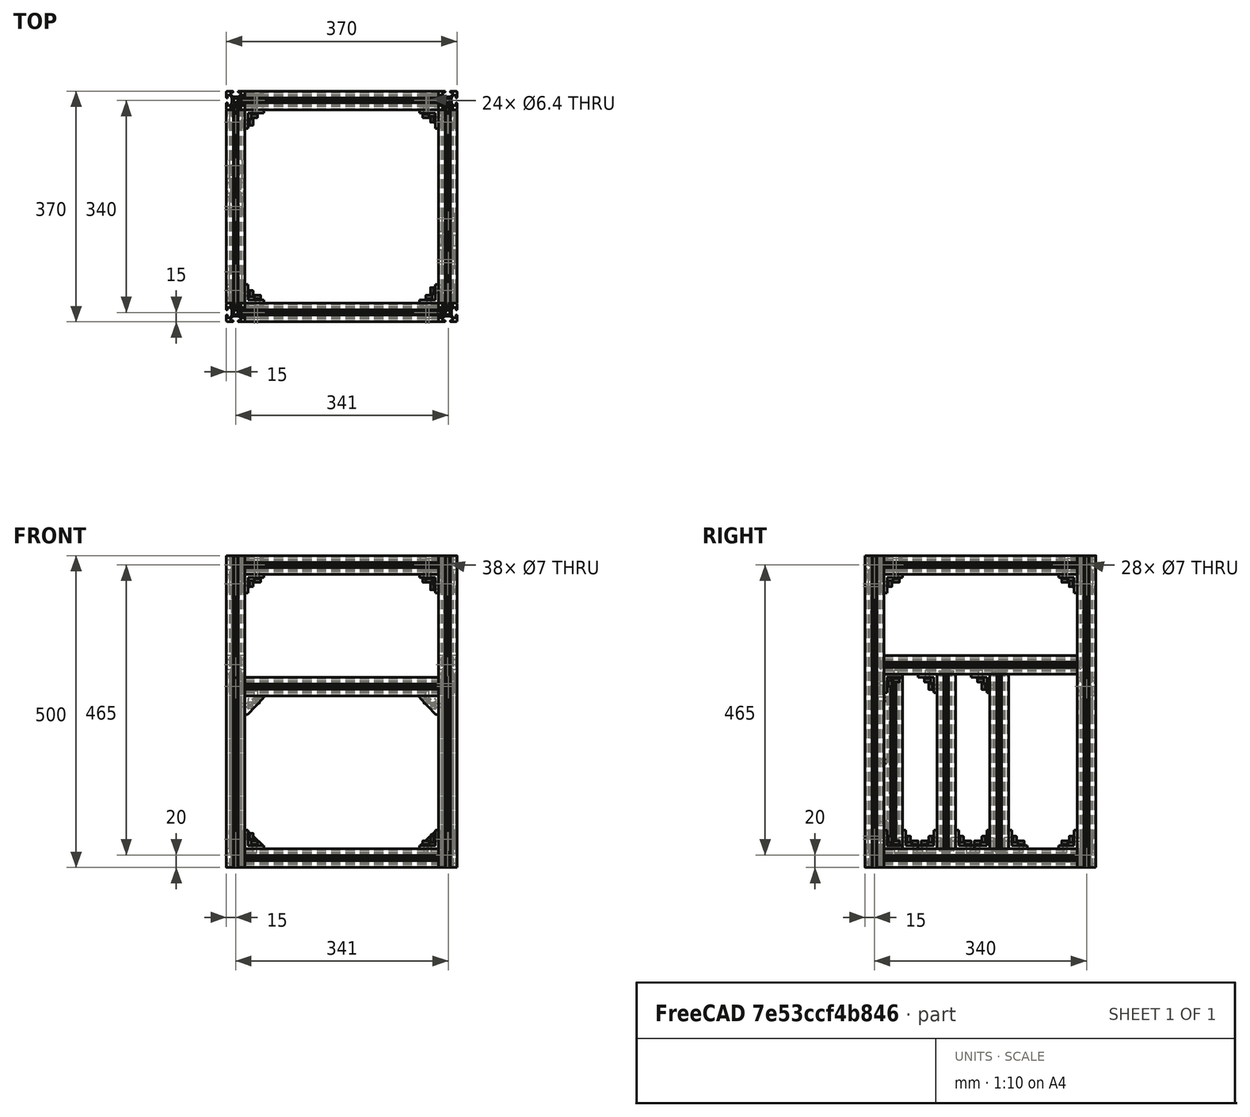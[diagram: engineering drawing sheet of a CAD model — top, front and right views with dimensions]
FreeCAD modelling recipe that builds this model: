
FCSTD DOCUMENT  (FreeCAD 0.19R24291 (Git))
Label: frame-assembly
License: Other
LicenseURL: GPL3
objects: Part::FeaturePython×141, Part::Feature×68, App::Part×4, PartDesign::CoordinateSystem×1
note: 210 computed .brp shape members not serialized (recipe doc carries the construction recipe); baked Part::Feature solids carry a one-line shape summary decoded from their .brp

FEATURE [Part::Feature] Extrude001  label="3030-310mm001-tap"
  Placement = pos=(-155,15,15) rot=(0,1,0;1.5708rad)
  shape: bbox 310 x 30 x 30 mm, 95 faces (baked)
FEATURE [Part::Feature] Extrude002  label="3030-310mm002-tap"
  Placement = pos=(-155,355,15) rot=(0,1,0;1.5708rad)
  shape: bbox 310 x 30 x 30 mm, 95 faces (baked)
FEATURE [Part::Feature] Extrude005  label="3030-310mm003-tap"
  Placement = pos=(170,30,485) rot=(0.57735,-0.57735,-0.57735;4.18879rad)
  shape: bbox 30 x 310 x 30 mm, 95 faces (baked)
FEATURE [Part::Feature] Extrude006  label="3030-310mm004-tap"
  Placement = pos=(-170,30,485) rot=(0.57735,-0.57735,-0.57735;4.18879rad)
  shape: bbox 30 x 310 x 30 mm, 95 faces (baked)
FEATURE [Part::Feature] Extrude007  label="3030-310mm005-tap"
  Placement = pos=(-155,355,485) rot=(0,1,0;1.5708rad)
  shape: bbox 310 x 30 x 30 mm, 95 faces (baked)
FEATURE [Part::Feature] Extrude008  label="3030-310mm006-tap"
  Placement = pos=(-155,15,485) rot=(0,1,0;1.5708rad)
  shape: bbox 310 x 30 x 30 mm, 95 faces (baked)
FEATURE [Part::Feature] Extrude010  label="3030-310mm007-tap"
  Placement = pos=(-155,355,290) rot=(0,1,0;1.5708rad)
  shape: bbox 310 x 30 x 30 mm, 95 faces (baked)
FEATURE [Part::Feature] Extrude002002002002  label="3030-280mm001-tap"
  Placement = pos=(-170,215,30) rot=(0,0,1;0rad)
  shape: bbox 30 x 30 x 280 mm, 95 faces (baked)
FEATURE [Part::Feature] Extrude002002002003  label="3030-280mm002-tap"
  Placement = pos=(170,130,30) rot=(0,0,1;0rad)
  shape: bbox 30 x 30 x 280 mm, 95 faces (baked)
FEATURE [Part::Feature] Cut008004003004014002002003  label="3030-280mm003-tap"
  Placement = pos=(-170,45,30) rot=(0,0,1;0rad)
  shape: bbox 30 x 30 x 280 mm, 137 faces (baked)
FEATURE [Part::Feature] Cut008004003004014002002011  label="3030-310mm008-tap-drill"
  Placement = pos=(-170,30,0) rot=(0,0,1;0rad)
  shape: bbox 30 x 310 x 30 mm, 109 faces (baked)
FEATURE [Part::Feature] Cut008004003004014002002012  label="3030-310mm009-tap-drill"
  Placement = pos=(-170,30,310) rot=(0,0,1;0rad)
  shape: bbox 30 x 310 x 30 mm, 109 faces (baked)
FEATURE [Part::Feature] Cut008004003004014002002013  label="3030-310mm010-tap-drill"
  Placement = pos=(170,30,0) rot=(0,0,1;0rad)
  shape: bbox 30 x 310 x 30 mm, 109 faces (baked)
FEATURE [Part::Feature] Cut008004003004014002002014  label="3030-310mm011-tap-drill"
  Placement = pos=(170,30,310) rot=(0,0,1;0rad)
  shape: bbox 30 x 310 x 30 mm, 109 faces (baked)
FEATURE [Part::Feature] Part__Feature112001022  label="Block-corner-bracket003"
  Placement = pos=(155,355,275) rot=(0.57735,0.57735,-0.57735;4.18879rad)
  shape: bbox 31 x 20 x 31 mm, 71 faces (baked)
FEATURE [Part::Feature] Part__Feature112001023  label="Block-corner-bracket004"
  Placement = pos=(-155,355,275) rot=(0.57735,-0.57735,0.57735;4.18879rad)
  shape: bbox 31 x 20 x 31 mm, 71 faces (baked)
FEATURE [Part::Feature] Part__Feature008  label="L-corner-bracket001"
  Placement = pos=(-155,15,30) rot=(0,0,-1;1.5708rad)
  shape: bbox 30 x 20 x 30 mm, 10 faces (baked)
FEATURE [Part::Feature] Part__Feature112001040  label="L-corner-bracket002"
  Placement = pos=(-155,15,470) rot=(0.57735,-0.57735,0.57735;4.18879rad)
  shape: bbox 30 x 20 x 30 mm, 10 faces (baked)
FEATURE [Part::Feature] Part__Feature112001041  label="L-corner-bracket003"
  Placement = pos=(155,15,470) rot=(0.707107,-0.707107,0;3.14159rad)
  shape: bbox 30 x 20 x 30 mm, 10 faces (baked)
FEATURE [Part::Feature] Part__Feature112001042  label="L-corner-bracket004"
  Placement = pos=(155,15,30) rot=(0.57735,-0.57735,-0.57735;2.0944rad)
  shape: bbox 30 x 20 x 30 mm, 10 faces (baked)
FEATURE [Part::Feature] Part__Feature112001054  label="HCJ_Joint001"
  Placement = pos=(-159,355,290) rot=(0.57735,0.57735,-0.57735;2.0944rad)
  shape: bbox 7.5 x 15 x 24 mm, 29 faces (baked)
FEATURE [Part::Feature] Part__Feature112001055  label="HCJ_Joint002"
  Placement = pos=(160,355,290) rot=(0.57735,-0.57735,-0.57735;4.18879rad)
  shape: bbox 7.5 x 15 x 24 mm, 29 faces (baked)
FEATURE [Part::Feature] Part__Feature112001056  label="HCJ_Joint003"
  Placement = pos=(-159,355,485) rot=(0.57735,0.57735,-0.57735;2.0944rad)
  shape: bbox 7.5 x 15 x 24 mm, 29 faces (baked)
FEATURE [Part::Feature] Part__Feature112001057  label="HCJ_Joint004"
  Placement = pos=(160,355,485) rot=(0.57735,-0.57735,-0.57735;4.18879rad)
  shape: bbox 7.5 x 15 x 24 mm, 29 faces (baked)
FEATURE [Part::Feature] Part__Feature112001058  label="HCJ_Joint005"
  Placement = pos=(-159,355,15) rot=(0.57735,0.57735,-0.57735;2.0944rad)
  shape: bbox 7.5 x 15 x 24 mm, 29 faces (baked)
FEATURE [Part::Feature] Part__Feature112001059  label="HCJ_Joint006"
  Placement = pos=(160,355,15) rot=(0.57735,-0.57735,-0.57735;4.18879rad)
  shape: bbox 7.5 x 15 x 24 mm, 29 faces (baked)
FEATURE [Part::Feature] Part__Feature112001060  label="HCJ_Joint007"
  Placement = pos=(170,344,15) rot=(0.707107,0,-0.707107;3.14159rad)
  shape: bbox 15 x 7.5 x 24 mm, 29 faces (baked)
FEATURE [Part::Feature] Part__Feature112001061  label="HCJ_Joint008"
  Placement = pos=(170,26,15) rot=(0,1,0;1.5708rad)
  shape: bbox 15 x 7.5 x 24 mm, 29 faces (baked)
FEATURE [Part::Feature] Part__Feature112001062  label="HCJ_Joint009"
  Placement = pos=(159,15,15) rot=(0.57735,-0.57735,-0.57735;4.18879rad)
  shape: bbox 7.5 x 15 x 24 mm, 29 faces (baked)
FEATURE [Part::Feature] Part__Feature112001063  label="HCJ_Joint010"
  Placement = pos=(-159,15,15) rot=(0.57735,0.57735,-0.57735;2.0944rad)
  shape: bbox 7.5 x 15 x 24 mm, 29 faces (baked)
FEATURE [Part::Feature] Part__Feature112001064  label="HCJ_Joint011"
  Placement = pos=(-170,26,15) rot=(0,1,0;1.5708rad)
  shape: bbox 15 x 7.5 x 24 mm, 29 faces (baked)
FEATURE [Part::Feature] Part__Feature112001065  label="HCJ_Joint012"
  Placement = pos=(-170,344,485) rot=(0.707107,0,-0.707107;3.14159rad)
  shape: bbox 15 x 7.5 x 24 mm, 29 faces (baked)
FEATURE [Part::Feature] Part__Feature112001066  label="HCJ_Joint013"
  Placement = pos=(170,344,485) rot=(0.707107,0,-0.707107;3.14159rad)
  shape: bbox 15 x 7.5 x 24 mm, 29 faces (baked)
FEATURE [Part::Feature] Part__Feature112001067  label="HCJ_Joint014"
  Placement = pos=(170,26,485) rot=(0,1,0;1.5708rad)
  shape: bbox 15 x 7.5 x 24 mm, 29 faces (baked)
FEATURE [Part::Feature] Part__Feature112001068  label="HCJ_Joint015"
  Placement = pos=(159,15,485) rot=(0.57735,-0.57735,-0.57735;4.18879rad)
  shape: bbox 7.5 x 15 x 24 mm, 29 faces (baked)
FEATURE [Part::Feature] Part__Feature112001069  label="HCJ_Joint016"
  Placement = pos=(-159,15,485) rot=(0.57735,0.57735,-0.57735;2.0944rad)
  shape: bbox 7.5 x 15 x 24 mm, 29 faces (baked)
FEATURE [Part::Feature] Part__Feature112001070  label="HCJ_Joint017"
  Placement = pos=(-170,26,485) rot=(0,1,0;1.5708rad)
  shape: bbox 15 x 7.5 x 24 mm, 29 faces (baked)
FEATURE [Part::Feature] Part__Feature112001071  label="L-corner-bracket005"
  Placement = pos=(-155,30,485) rot=(0,1,0;1.5708rad)
  shape: bbox 30 x 30 x 20 mm, 10 faces (baked)
FEATURE [Part::Feature] Part__Feature112001072  label="L-corner-bracket006"
  Placement = pos=(-155,340,485) rot=(0.57735,0.57735,-0.57735;2.0944rad)
  shape: bbox 30 x 30 x 20 mm, 10 faces (baked)
FEATURE [Part::Feature] Part__Feature112001073  label="L-corner-bracket007"
  Placement = pos=(155,340,485) rot=(0.707107,0,-0.707107;3.14159rad)
  shape: bbox 30 x 30 x 20 mm, 10 faces (baked)
FEATURE [Part::Feature] Part__Feature112001074  label="L-corner-bracket008"
  Placement = pos=(155,30,485) rot=(0.57735,-0.57735,-0.57735;4.18879rad)
  shape: bbox 30 x 30 x 20 mm, 10 faces (baked)
FEATURE [Part::Feature] Part__Feature112001020  label="Block-corner-bracket001"
  Placement = pos=(-155,355,30) rot=(0,0,-1;1.5708rad)
  shape: bbox 31 x 20 x 31 mm, 71 faces (baked)
FEATURE [Part::Feature] Part__Feature112001021  label="Block-corner-bracket002"
  Placement = pos=(155,355,30) rot=(0,0,1;1.5708rad)
  shape: bbox 31 x 20 x 31 mm, 71 faces (baked)
FEATURE [Part::Feature] Part__Feature112001075  label="L-corner-bracket009"
  Placement = pos=(155,355,470) rot=(0.57735,0.57735,-0.57735;4.18879rad)
  shape: bbox 30 x 20 x 30 mm, 10 faces (baked)
FEATURE [Part::Feature] Part__Feature112001078  label="L-corner-bracket011"
  Placement = pos=(170,30,30) rot=(0,0.707107,0.707107;3.14159rad)
  shape: bbox 20 x 30 x 30 mm, 10 faces (baked)
FEATURE [Part::Feature] Part__Feature112001079  label="L-corner-bracket012"
  Placement = pos=(-170,200,30) rot=(1,0,0;1.5708rad)
  shape: bbox 20 x 30 x 30 mm, 10 faces (baked)
FEATURE [Part::Feature] Part__Feature112001080  label="L-corner-bracket013"
  Placement = pos=(171,115,30) rot=(1,0,0;1.5708rad)
  shape: bbox 20 x 30 x 30 mm, 10 faces (baked)
FEATURE [Part::Feature] Part__Feature112001081  label="L-corner-bracket014"
  Placement = pos=(-170,200,310) rot=(1,0,0;3.14159rad)
  shape: bbox 20 x 30 x 30 mm, 10 faces (baked)
FEATURE [Part::Feature] Part__Feature112001082  label="L-corner-bracket016"
  Placement = pos=(171,115,310) rot=(1,0,0;3.14159rad)
  shape: bbox 20 x 30 x 30 mm, 10 faces (baked)
FEATURE [Part::Feature] Part__Feature112001083  label="L-corner-bracket015"
  Placement = pos=(171,30,310) rot=(-1,0,0;1.5708rad)
  shape: bbox 20 x 30 x 30 mm, 10 faces (baked)
FEATURE [Part::Feature] Part__Feature112001084  label="L-corner-bracket018"
  Placement = pos=(171,145,30) rot=(0,0.707107,0.707107;3.14159rad)
  shape: bbox 20 x 30 x 30 mm, 10 faces (baked)
FEATURE [Part::Feature] Part__Feature112001085  label="L-corner-bracket017"
  Placement = pos=(-170,230,30) rot=(0,0.707107,0.707107;3.14159rad)
  shape: bbox 20 x 30 x 30 mm, 10 faces (baked)
FEATURE [Part::Feature] Part__Feature112001086  label="L-corner-bracket020"
  Placement = pos=(-170,60,30) rot=(0,0.707107,0.707107;3.14159rad)
  shape: bbox 20 x 30 x 30 mm, 10 faces (baked)
FEATURE [Part::Feature] Part__Feature112001087  label="HCJ_Joint018"
  Placement = pos=(-170,344,15) rot=(0.707107,0,-0.707107;3.14159rad)
  shape: bbox 15 x 7.5 x 24 mm, 29 faces (baked)
FEATURE [Part::Feature] Part__Feature112001089  label="HCJ_Joint019"
  Placement = pos=(-170,214.5,27) rot=(0.57735,-0.57735,-0.57735;2.0944rad)
  shape: bbox 15 x 24 x 7.5 mm, 29 faces (baked)
FEATURE [Part::Feature] Part__Feature112001090  label="HCJ_Joint020"
  Placement = pos=(-170,214.5,315) rot=(0.57735,0.57735,-0.57735;4.18879rad)
  shape: bbox 15 x 24 x 7.5 mm, 29 faces (baked)
FEATURE [Part::Feature] Part__Feature112001091  label="HCJ_Joint021"
  Placement = pos=(170,130.5,315) rot=(0.57735,0.57735,-0.57735;4.18879rad)
  shape: bbox 15 x 24 x 7.5 mm, 29 faces (baked)
FEATURE [Part::Feature] Part__Feature112001092  label="HCJ_Joint022"
  Placement = pos=(170,130.5,27) rot=(0.57735,-0.57735,-0.57735;2.0944rad)
  shape: bbox 15 x 24 x 7.5 mm, 29 faces (baked)
FEATURE [App::Part] Part049  label="HCJ-joint"
  Group = -> [Part__Feature112001054,Part__Feature112001055,Part__Feature112001056,Part__Feature112001057,Part__Feature112001058,Part__Feature112001059,Part__Feature112001060,Part__Feature112001061,Part__Feature112001062,Part__Feature112001063,Part__Feature112001064,Part__Feature112001065,Part__Feature112001066,Part__Feature112001067,Part__Feature112001068,Part__Feature112001069,Part__Feature112001070,+5 more]
  Origin = -> Origin051
FEATURE [Part::Feature] Part__Feature112001088  label="L-corner-bracket021"
  Placement = pos=(171,340,30) rot=(1,0,0;1.5708rad)
  shape: bbox 20 x 30 x 30 mm, 10 faces (baked)
FEATURE [Part::FeaturePython] Screw  label="M8x20-Screw"  # Fasteners workbench fastener (typed FeaturePython)
  Placement = pos=(170,344,485) rot=(-1,0,0;1.5708rad)
  baseObject = -> Extrude005 [Edge279]
  diameter = 5
  invert = false
  length = 3
  lengthCustom = 20
  matchOuter = false
  offset = 4
  thread = false
  type = 39
FEATURE [Part::FeaturePython] Screw001  label="M8x20-Screw057"  # Fasteners workbench fastener (typed FeaturePython)
  Placement = pos=(159,355,485) rot=(0,1,0;1.5708rad)
  baseObject = -> Extrude007 [Edge279]
  diameter = 5
  invert = false
  length = 3
  lengthCustom = 20
  matchOuter = false
  offset = 4
  thread = false
  type = 39
FEATURE [Part::FeaturePython] Screw002  label="M8x20-Screw007"  # Fasteners workbench fastener (typed FeaturePython)
  Placement = pos=(170,344,325) rot=(-1,0,0;1.5708rad)
  baseObject = -> Cut008004003004014002002014 [Edge190]
  diameter = 5
  invert = false
  length = 3
  lengthCustom = 20
  matchOuter = false
  offset = 4
  thread = false
  type = 39
FEATURE [Part::FeaturePython] Screw003  label="M8x20-Screw008"  # Fasteners workbench fastener (typed FeaturePython)
  Placement = pos=(159,355,290) rot=(0,1,0;1.5708rad)
  baseObject = -> Extrude010 [Edge279]
  diameter = 5
  invert = false
  length = 3
  lengthCustom = 20
  matchOuter = false
  offset = 4
  thread = false
  type = 39
FEATURE [Part::FeaturePython] Screw004  label="M8x20-Screw009"  # Fasteners workbench fastener (typed FeaturePython)
  Placement = pos=(170,344,15) rot=(-1,0,0;1.5708rad)
  baseObject = -> Cut008004003004014002002013 [Edge190]
  diameter = 5
  invert = false
  length = 3
  lengthCustom = 20
  matchOuter = false
  offset = 4
  thread = false
  type = 39
FEATURE [Part::FeaturePython] Screw005  label="M8x20-Screw010"  # Fasteners workbench fastener (typed FeaturePython)
  Placement = pos=(159,355,15) rot=(0,1,0;1.5708rad)
  baseObject = -> Extrude002 [Edge279]
  diameter = 5
  invert = false
  length = 3
  lengthCustom = 20
  matchOuter = false
  offset = 4
  thread = false
  type = 39
FEATURE [Part::FeaturePython] Screw006  label="M8x20-Screw058"  # Fasteners workbench fastener (typed FeaturePython)
  Placement = pos=(-159,355,485) rot=(0,-1,0;1.5708rad)
  baseObject = -> Extrude007 [Edge278]
  diameter = 5
  invert = true
  length = 3
  lengthCustom = 20
  matchOuter = false
  offset = 4
  thread = false
  type = 39
FEATURE [Part::FeaturePython] Screw007  label="M8x20-Screw054"  # Fasteners workbench fastener (typed FeaturePython)
  Placement = pos=(-170,344,485) rot=(-1,0,0;1.5708rad)
  baseObject = -> Extrude006 [Edge279]
  diameter = 5
  invert = false
  length = 3
  lengthCustom = 20
  matchOuter = false
  offset = 4
  thread = false
  type = 39
FEATURE [Part::FeaturePython] Screw008  label="M8x20-Screw019"  # Fasteners workbench fastener (typed FeaturePython)
  Placement = pos=(-170,344,325) rot=(-1,0,0;1.5708rad)
  baseObject = -> Cut008004003004014002002012 [Edge190]
  diameter = 5
  invert = false
  length = 3
  lengthCustom = 20
  matchOuter = false
  offset = 4
  thread = false
  type = 39
FEATURE [Part::FeaturePython] Screw009  label="M8x20-Screw024"  # Fasteners workbench fastener (typed FeaturePython)
  Placement = pos=(-159,355,290) rot=(0,-1,0;1.5708rad)
  baseObject = -> Extrude010 [Edge278]
  diameter = 5
  invert = true
  length = 3
  lengthCustom = 20
  matchOuter = false
  offset = 4
  thread = false
  type = 39
FEATURE [Part::FeaturePython] Screw010  label="M8x20-Screw025"  # Fasteners workbench fastener (typed FeaturePython)
  Placement = pos=(-159,355,15) rot=(0,-1,0;1.5708rad)
  baseObject = -> Extrude002 [Edge278]
  diameter = 5
  invert = true
  length = 3
  lengthCustom = 20
  matchOuter = false
  offset = 4
  thread = false
  type = 39
FEATURE [Part::FeaturePython] Screw011  label="M8x20-Screw022"  # Fasteners workbench fastener (typed FeaturePython)
  Placement = pos=(-170,344,15) rot=(-1,0,0;1.5708rad)
  baseObject = -> Cut008004003004014002002011 [Edge190]
  diameter = 5
  invert = false
  length = 3
  lengthCustom = 20
  matchOuter = false
  offset = 4
  thread = false
  type = 39
FEATURE [Part::FeaturePython] Screw012  label="M8x20-Screw053"  # Fasteners workbench fastener (typed FeaturePython)
  Placement = pos=(-170,26,485) rot=(1,0,0;1.5708rad)
  baseObject = -> Extrude006 [Edge278]
  diameter = 5
  invert = true
  length = 15
  lengthCustom = 20
  matchOuter = false
  offset = 4
  thread = false
  type = 39
FEATURE [Part::FeaturePython] Screw013  label="M8x20-Screw055"  # Fasteners workbench fastener (typed FeaturePython)
  Placement = pos=(-159,15,485) rot=(0,-1,0;1.5708rad)
  baseObject = -> Extrude008 [Edge278]
  diameter = 5
  invert = true
  length = 15
  lengthCustom = 20
  matchOuter = false
  offset = 4
  thread = false
  type = 39
FEATURE [Part::FeaturePython] Screw014  label="M8x20-Screw033"  # Fasteners workbench fastener (typed FeaturePython)
  Placement = pos=(-170,26,325) rot=(1,0,0;1.5708rad)
  baseObject = -> Cut008004003004014002002012 [Edge100]
  diameter = 5
  invert = true
  length = 15
  lengthCustom = 20
  matchOuter = false
  offset = 4
  thread = false
  type = 39
FEATURE [Part::FeaturePython] Screw015  label="M8x20-Screw034"  # Fasteners workbench fastener (typed FeaturePython)
  Placement = pos=(-170,26,15) rot=(1,0,0;1.5708rad)
  baseObject = -> Cut008004003004014002002011 [Edge100]
  diameter = 5
  invert = true
  length = 15
  lengthCustom = 20
  matchOuter = false
  offset = 4
  thread = false
  type = 39
FEATURE [Part::FeaturePython] Screw016  label="M8x20-Screw035"  # Fasteners workbench fastener (typed FeaturePython)
  Placement = pos=(-159,15,15) rot=(0,-1,0;1.5708rad)
  baseObject = -> Extrude001 [Edge278]
  diameter = 5
  invert = true
  length = 15
  lengthCustom = 20
  matchOuter = false
  offset = 4
  thread = false
  type = 39
FEATURE [Part::FeaturePython] Screw017  label="M8x20-Screw056"  # Fasteners workbench fastener (typed FeaturePython)
  Placement = pos=(159,15,485) rot=(0,1,0;1.5708rad)
  baseObject = -> Extrude008 [Edge279]
  diameter = 5
  invert = false
  length = 3
  lengthCustom = 20
  matchOuter = false
  offset = 4
  thread = false
  type = 39
FEATURE [Part::FeaturePython] Screw018  label="M8x20-Screw059"  # Fasteners workbench fastener (typed FeaturePython)
  Placement = pos=(170,26,485) rot=(1,0,0;1.5708rad)
  baseObject = -> Extrude005 [Edge278]
  diameter = 5
  invert = true
  length = 3
  lengthCustom = 20
  matchOuter = false
  offset = 4
  thread = false
  type = 39
FEATURE [Part::FeaturePython] Screw019  label="M8x20-Screw047"  # Fasteners workbench fastener (typed FeaturePython)
  Placement = pos=(170,26,325) rot=(1,0,0;1.5708rad)
  baseObject = -> Cut008004003004014002002014 [Edge100]
  diameter = 5
  invert = true
  length = 3
  lengthCustom = 20
  matchOuter = false
  offset = 4
  thread = false
  type = 39
FEATURE [Part::FeaturePython] Screw020  label="M8x20-Screw044"  # Fasteners workbench fastener (typed FeaturePython)
  Placement = pos=(159,15,15) rot=(0,1,0;1.5708rad)
  baseObject = -> Extrude001 [Edge279]
  diameter = 5
  invert = false
  length = 3
  lengthCustom = 20
  matchOuter = false
  offset = 4
  thread = false
  type = 39
FEATURE [Part::FeaturePython] Screw021  label="M8x20-Screw048"  # Fasteners workbench fastener (typed FeaturePython)
  Placement = pos=(170,26,15) rot=(1,0,0;1.5708rad)
  baseObject = -> Cut008004003004014002002013 [Edge100]
  diameter = 5
  invert = true
  length = 3
  lengthCustom = 20
  matchOuter = false
  offset = 4
  thread = false
  type = 39
FEATURE [Part::FeaturePython] Washer  label="M6-Washer"  # Fasteners workbench fastener (typed FeaturePython)
  Placement = pos=(-150,15,455) rot=(0,1,0;1.5708rad)
  baseObject = -> Part__Feature112001040 [Edge7]
  diameter = 2
  invert = true
  matchOuter = true
  offset = 0
  type = 4
FEATURE [Part::FeaturePython] Washer001  label="M6-Washer119"  # Fasteners workbench fastener (typed FeaturePython)
  Placement = pos=(-135,15,465) rot=(1,0,0;3.14159rad)
  baseObject = -> Part__Feature112001040 [Edge1]
  diameter = 2
  invert = true
  matchOuter = true
  offset = 0
  type = 4
FEATURE [Part::FeaturePython] Washer002  label="M6-Washer114"  # Fasteners workbench fastener (typed FeaturePython)
  Placement = pos=(140,15,465) rot=(1,0,0;3.14159rad)
  baseObject = -> Part__Feature112001041 [Edge7]
  diameter = 2
  invert = true
  matchOuter = true
  offset = 0
  type = 4
FEATURE [Part::FeaturePython] Washer003  label="M6-Washer113"  # Fasteners workbench fastener (typed FeaturePython)
  Placement = pos=(150,15,450) rot=(0,-1,0;1.5708rad)
  baseObject = -> Part__Feature112001041 [Edge1]
  diameter = 2
  invert = true
  matchOuter = true
  offset = 0
  type = 4
FEATURE [Part::FeaturePython] Washer004  label="M6-Washer011"  # Fasteners workbench fastener (typed FeaturePython)
  Placement = pos=(150,15,45) rot=(0,-1,0;1.5708rad)
  baseObject = -> Part__Feature112001042 [Edge7]
  diameter = 2
  invert = true
  matchOuter = true
  offset = 0
  type = 4
FEATURE [Part::FeaturePython] Washer005  label="M6-Washer012"  # Fasteners workbench fastener (typed FeaturePython)
  Placement = pos=(135,15,35) rot=(0,0,1;0rad)
  baseObject = -> Part__Feature112001042 [Edge1]
  diameter = 2
  invert = true
  matchOuter = true
  offset = 0
  type = 4
FEATURE [Part::FeaturePython] Washer006  label="M6-Washer013"  # Fasteners workbench fastener (typed FeaturePython)
  Placement = pos=(-150,15,50) rot=(0,1,0;1.5708rad)
  baseObject = -> Part__Feature008 [Edge4]
  diameter = 2
  invert = true
  matchOuter = true
  offset = 0
  type = 4
FEATURE [Part::FeaturePython] Washer007  label="M6-Washer014"  # Fasteners workbench fastener (typed FeaturePython)
  Placement = pos=(-140,15,35) rot=(0,0,1;0rad)
  baseObject = -> Part__Feature008 [Edge7]
  diameter = 2
  invert = true
  matchOuter = true
  offset = 0
  type = 4
FEATURE [Part::FeaturePython] Washer008  label="M6-Washer027"  # Fasteners workbench fastener (typed FeaturePython)
  Placement = pos=(171,50,305) rot=(1,0,0;3.14159rad)
  baseObject = -> Part__Feature112001083 [Edge1]
  diameter = 2
  invert = true
  matchOuter = true
  offset = 0
  type = 4
FEATURE [Part::FeaturePython] Washer009  label="M6-Washer028"  # Fasteners workbench fastener (typed FeaturePython)
  Placement = pos=(171,35,295) rot=(-1,0,0;1.5708rad)
  baseObject = -> Part__Feature112001083 [Edge7]
  diameter = 2
  invert = true
  matchOuter = true
  offset = 0
  type = 4
FEATURE [Part::FeaturePython] Washer010  label="M6-Washer029"  # Fasteners workbench fastener (typed FeaturePython)
  Placement = pos=(171,100,305) rot=(1,0,0;3.14159rad)
  baseObject = -> Part__Feature112001082 [Edge7]
  diameter = 2
  invert = true
  matchOuter = true
  offset = 0
  type = 4
FEATURE [Part::FeaturePython] Washer011  label="M6-Washer030"  # Fasteners workbench fastener (typed FeaturePython)
  Placement = pos=(171,110,290) rot=(1,0,0;1.5708rad)
  baseObject = -> Part__Feature112001082 [Edge1]
  diameter = 2
  invert = true
  matchOuter = true
  offset = 0
  type = 4
FEATURE [Part::FeaturePython] Washer012  label="M6-Washer031"  # Fasteners workbench fastener (typed FeaturePython)
  Placement = pos=(170,35,45) rot=(-1,0,0;1.5708rad)
  baseObject = -> Part__Feature112001078 [Edge7]
  diameter = 2
  invert = true
  matchOuter = true
  offset = 0
  type = 4
FEATURE [Part::FeaturePython] Washer013  label="M6-Washer032"  # Fasteners workbench fastener (typed FeaturePython)
  Placement = pos=(170,50,35) rot=(0,0,1;0rad)
  baseObject = -> Part__Feature112001078 [Edge1]
  diameter = 2
  invert = true
  matchOuter = true
  offset = 0
  type = 4
FEATURE [Part::FeaturePython] Washer014  label="M6-Washer033"  # Fasteners workbench fastener (typed FeaturePython)
  Placement = pos=(171,95,35) rot=(0,0,1;0rad)
  baseObject = -> Part__Feature112001080 [Edge4]
  diameter = 2
  invert = true
  matchOuter = true
  offset = 0
  type = 4
FEATURE [Part::FeaturePython] Washer015  label="M6-Washer034"  # Fasteners workbench fastener (typed FeaturePython)
  Placement = pos=(171,110,45) rot=(1,0,0;1.5708rad)
  baseObject = -> Part__Feature112001080 [Edge7]
  diameter = 2
  invert = true
  matchOuter = true
  offset = 0
  type = 4
FEATURE [Part::FeaturePython] Washer016  label="M6-Washer035"  # Fasteners workbench fastener (typed FeaturePython)
  Placement = pos=(171,165,35) rot=(0,0,1;0rad)
  baseObject = -> Part__Feature112001084 [Edge4]
  diameter = 2
  invert = true
  matchOuter = true
  offset = 0
  type = 4
FEATURE [Part::FeaturePython] Washer017  label="M6-Washer036"  # Fasteners workbench fastener (typed FeaturePython)
  Placement = pos=(171,150,45) rot=(-1,0,0;1.5708rad)
  baseObject = -> Part__Feature112001084 [Edge7]
  diameter = 2
  invert = true
  matchOuter = true
  offset = 0
  type = 4
FEATURE [Part::FeaturePython] Washer018  label="M6-Washer037"  # Fasteners workbench fastener (typed FeaturePython)
  Placement = pos=(171,320,35) rot=(0,0,1;0rad)
  baseObject = -> Part__Feature112001088 [Edge1]
  diameter = 2
  invert = true
  matchOuter = true
  offset = 0
  type = 4
FEATURE [Part::FeaturePython] Washer019  label="M6-Washer038"  # Fasteners workbench fastener (typed FeaturePython)
  Placement = pos=(171,335,45) rot=(1,0,0;1.5708rad)
  baseObject = -> Part__Feature112001088 [Edge7]
  diameter = 2
  invert = true
  matchOuter = true
  offset = 0
  type = 4
FEATURE [Part::FeaturePython] Washer020  label="M6-Washer039"  # Fasteners workbench fastener (typed FeaturePython)
  Placement = pos=(137,355,270.8) rot=(1,0,0;3.14159rad)
  baseObject = -> Part__Feature112001022 [Edge154]
  diameter = 2
  invert = false
  matchOuter = true
  offset = 0
  type = 4
FEATURE [Part::FeaturePython] Washer021  label="M6-Washer040"  # Fasteners workbench fastener (typed FeaturePython)
  Placement = pos=(150.5,355,260) rot=(0,-1,0;1.5708rad)
  baseObject = -> Part__Feature112001022 [Edge155]
  diameter = 2
  invert = false
  matchOuter = true
  offset = 0
  type = 4
FEATURE [Part::FeaturePython] Washer022  label="M6-Washer041"  # Fasteners workbench fastener (typed FeaturePython)
  Placement = pos=(140,355,34.5) rot=(0,0,1;0rad)
  baseObject = -> Part__Feature112001021 [Edge157]
  diameter = 2
  invert = false
  matchOuter = true
  offset = 0
  type = 4
FEATURE [Part::FeaturePython] Washer023  label="M6-Washer042"  # Fasteners workbench fastener (typed FeaturePython)
  Placement = pos=(150.8,355,48) rot=(0,-1,0;1.5708rad)
  baseObject = -> Part__Feature112001021 [Edge154]
  diameter = 2
  invert = false
  matchOuter = true
  offset = 0
  type = 4
FEATURE [Part::FeaturePython] Washer024  label="M6-Washer043"  # Fasteners workbench fastener (typed FeaturePython)
  Placement = pos=(-140,355,34.5) rot=(0,0,1;0rad)
  baseObject = -> Part__Feature112001020 [Edge155]
  diameter = 2
  invert = false
  matchOuter = true
  offset = 0
  type = 4
FEATURE [Part::FeaturePython] Washer025  label="M6-Washer044"  # Fasteners workbench fastener (typed FeaturePython)
  Placement = pos=(-150.8,355,48) rot=(0,1,0;1.5708rad)
  baseObject = -> Part__Feature112001020 [Edge153]
  diameter = 2
  invert = false
  matchOuter = true
  offset = 0
  type = 4
FEATURE [Part::FeaturePython] Washer026  label="M6-Washer045"  # Fasteners workbench fastener (typed FeaturePython)
  Placement = pos=(-150.5,355,260) rot=(0,1,0;1.5708rad)
  baseObject = -> Part__Feature112001023 [Edge155]
  diameter = 2
  invert = false
  matchOuter = true
  offset = 0
  type = 4
FEATURE [Part::FeaturePython] Washer027  label="M6-Washer046"  # Fasteners workbench fastener (typed FeaturePython)
  Placement = pos=(-137,355,270.8) rot=(1,0,0;3.14159rad)
  baseObject = -> Part__Feature112001023 [Edge153]
  diameter = 2
  invert = false
  matchOuter = true
  offset = 0
  type = 4
FEATURE [Part::FeaturePython] Washer028  label="M6-Washer055"  # Fasteners workbench fastener (typed FeaturePython)
  Placement = pos=(-170,235,45) rot=(-1,0,0;1.5708rad)
  baseObject = -> Part__Feature112001085 [Edge7]
  diameter = 2
  invert = true
  matchOuter = true
  offset = 0
  type = 4
FEATURE [Part::FeaturePython] Washer029  label="M6-Washer056"  # Fasteners workbench fastener (typed FeaturePython)
  Placement = pos=(-170,250,35) rot=(0,0,1;0rad)
  baseObject = -> Part__Feature112001085 [Edge1]
  diameter = 2
  invert = true
  matchOuter = true
  offset = 0
  type = 4
FEATURE [Part::FeaturePython] Washer030  label="M6-Washer057"  # Fasteners workbench fastener (typed FeaturePython)
  Placement = pos=(-170,180,35) rot=(0,0,1;0rad)
  baseObject = -> Part__Feature112001079 [Edge4]
  diameter = 2
  invert = true
  matchOuter = true
  offset = 0
  type = 4
FEATURE [Part::FeaturePython] Washer031  label="M6-Washer058"  # Fasteners workbench fastener (typed FeaturePython)
  Placement = pos=(-170,195,45) rot=(1,0,0;1.5708rad)
  baseObject = -> Part__Feature112001079 [Edge7]
  diameter = 2
  invert = true
  matchOuter = true
  offset = 0
  type = 4
FEATURE [Part::FeaturePython] Washer032  label="M6-Washer059"  # Fasteners workbench fastener (typed FeaturePython)
  Placement = pos=(-170,80,35) rot=(0,0,1;0rad)
  baseObject = -> Part__Feature112001086 [Edge1]
  diameter = 2
  invert = true
  matchOuter = true
  offset = 0
  type = 4
FEATURE [Part::FeaturePython] Washer033  label="M6-Washer060"  # Fasteners workbench fastener (typed FeaturePython)
  Placement = pos=(-170,65,45) rot=(-1,0,0;1.5708rad)
  baseObject = -> Part__Feature112001086 [Edge7]
  diameter = 2
  invert = true
  matchOuter = true
  offset = 0
  type = 4
FEATURE [Part::FeaturePython] Washer034  label="M6-Washer061"  # Fasteners workbench fastener (typed FeaturePython)
  Placement = pos=(-170,195,290) rot=(1,0,0;1.5708rad)
  baseObject = -> Part__Feature112001081 [Edge4]
  diameter = 2
  invert = true
  matchOuter = true
  offset = 0
  type = 4
FEATURE [Part::FeaturePython] Washer035  label="M6-Washer062"  # Fasteners workbench fastener (typed FeaturePython)
  Placement = pos=(-170,185,305) rot=(1,0,0;3.14159rad)
  baseObject = -> Part__Feature112001081 [Edge7]
  diameter = 2
  invert = true
  matchOuter = true
  offset = 0
  type = 4
FEATURE [Part::FeaturePython] Washer036  label="M6-Washer105"  # Fasteners workbench fastener (typed FeaturePython)
  Placement = pos=(135,335,485) rot=(1,0,0;1.5708rad)
  baseObject = -> Part__Feature112001073 [Edge1]
  diameter = 2
  invert = true
  matchOuter = true
  offset = 0
  type = 4
FEATURE [Part::FeaturePython] Washer037  label="M6-Washer106"  # Fasteners workbench fastener (typed FeaturePython)
  Placement = pos=(150,325,485) rot=(0,-1,0;1.5708rad)
  baseObject = -> Part__Feature112001073 [Edge7]
  diameter = 2
  invert = true
  matchOuter = true
  offset = 0
  type = 4
FEATURE [Part::FeaturePython] Washer038  label="M6-Washer112"  # Fasteners workbench fastener (typed FeaturePython)
  Placement = pos=(150,50,485) rot=(0,-1,0;1.5708rad)
  baseObject = -> Part__Feature112001074 [Edge1]
  diameter = 2
  invert = true
  matchOuter = true
  offset = 0
  type = 4
FEATURE [Part::FeaturePython] Washer039  label="M6-Washer111"  # Fasteners workbench fastener (typed FeaturePython)
  Placement = pos=(140,35,485) rot=(-1,0,0;1.5708rad)
  baseObject = -> Part__Feature112001074 [Edge7]
  diameter = 2
  invert = true
  matchOuter = true
  offset = 0
  type = 4
FEATURE [Part::FeaturePython] Washer040  label="M6-Washer116"  # Fasteners workbench fastener (typed FeaturePython)
  Placement = pos=(-135,35,485) rot=(-1,0,0;1.5708rad)
  baseObject = -> Part__Feature112001071 [Edge4]
  diameter = 2
  invert = true
  matchOuter = true
  offset = 0
  type = 4
FEATURE [Part::FeaturePython] Washer041  label="M6-Washer115"  # Fasteners workbench fastener (typed FeaturePython)
  Placement = pos=(-150,45,485) rot=(0,1,0;1.5708rad)
  baseObject = -> Part__Feature112001071 [Edge7]
  diameter = 2
  invert = true
  matchOuter = true
  offset = 0
  type = 4
FEATURE [Part::FeaturePython] Washer042  label="M6-Washer100"  # Fasteners workbench fastener (typed FeaturePython)
  Placement = pos=(-150,320,485) rot=(0,1,0;1.5708rad)
  baseObject = -> Part__Feature112001072 [Edge4]
  diameter = 2
  invert = true
  matchOuter = true
  offset = 0
  type = 4
FEATURE [Part::FeaturePython] Washer043  label="M6-Washer099"  # Fasteners workbench fastener (typed FeaturePython)
  Placement = pos=(-140,335,485) rot=(1,0,0;1.5708rad)
  baseObject = -> Part__Feature112001072 [Edge7]
  diameter = 2
  invert = true
  matchOuter = true
  offset = 0
  type = 4
FEATURE [Part::FeaturePython] Screw022  label="M6x14-Screw007"  # Fasteners workbench fastener (typed FeaturePython)
  Placement = pos=(-148.2,15,50) rot=(0,1,0;1.5708rad)
  baseObject = -> Washer006 [Edge1]
  diameter = 7
  invert = false
  length = 3
  lengthCustom = 14
  matchOuter = true
  offset = 0
  thread = false
  type = 33
FEATURE [Part::FeaturePython] Screw023  label="M6x14-Screw006"  # Fasteners workbench fastener (typed FeaturePython)
  Placement = pos=(-140,15,36.8) rot=(0,0,1;0rad)
  baseObject = -> Washer007 [Edge1]
  diameter = 7
  invert = false
  length = 3
  lengthCustom = 14
  matchOuter = true
  offset = 0
  thread = false
  type = 33
FEATURE [Part::FeaturePython] Screw024  label="M6x14-Screw005"  # Fasteners workbench fastener (typed FeaturePython)
  Placement = pos=(135,15,36.8) rot=(0,0,1;0rad)
  baseObject = -> Washer005 [Edge1]
  diameter = 7
  invert = false
  length = 3
  lengthCustom = 14
  matchOuter = true
  offset = 0
  thread = false
  type = 33
FEATURE [Part::FeaturePython] Screw025  label="M6x14-Screw004"  # Fasteners workbench fastener (typed FeaturePython)
  Placement = pos=(148.2,15,45) rot=(0,-1,0;1.5708rad)
  baseObject = -> Washer004 [Edge1]
  diameter = 7
  invert = false
  length = 3
  lengthCustom = 14
  matchOuter = true
  offset = 0
  thread = false
  type = 33
FEATURE [Part::FeaturePython] Screw026  label="M6x14-Screw074"  # Fasteners workbench fastener (typed FeaturePython)
  Placement = pos=(148.2,15,450) rot=(0,-1,0;1.5708rad)
  baseObject = -> Washer003 [Edge1]
  diameter = 7
  invert = false
  length = 3
  lengthCustom = 14
  matchOuter = true
  offset = 0
  thread = false
  type = 33
FEATURE [Part::FeaturePython] Screw027  label="M6x14-Screw075"  # Fasteners workbench fastener (typed FeaturePython)
  Placement = pos=(140,15,463.2) rot=(1,0,0;3.14159rad)
  baseObject = -> Washer002 [Edge1]
  diameter = 7
  invert = false
  length = 3
  lengthCustom = 14
  matchOuter = true
  offset = 0
  thread = false
  type = 33
FEATURE [Part::FeaturePython] Screw028  label="M6x14-Screw"  # Fasteners workbench fastener (typed FeaturePython)
  Placement = pos=(-135,15,463.2) rot=(1,0,0;3.14159rad)
  baseObject = -> Washer001 [Edge1]
  diameter = 7
  invert = false
  length = 3
  lengthCustom = 14
  matchOuter = true
  offset = 0
  thread = false
  type = 33
FEATURE [Part::FeaturePython] Screw029  label="M6x14-Screw080"  # Fasteners workbench fastener (typed FeaturePython)
  Placement = pos=(-148.2,15,455) rot=(0,1,0;1.5708rad)
  baseObject = -> Washer [Edge1]
  diameter = 7
  invert = false
  length = 3
  lengthCustom = 14
  matchOuter = true
  offset = 0
  thread = false
  type = 33
FEATURE [Part::FeaturePython] Screw030  label="M6x14-Screw015"  # Fasteners workbench fastener (typed FeaturePython)
  Placement = pos=(171,95,36.8) rot=(0,0,1;0rad)
  baseObject = -> Washer014 [Edge1]
  diameter = 7
  invert = false
  length = 3
  lengthCustom = 14
  matchOuter = true
  offset = 0
  thread = false
  type = 33
FEATURE [Part::FeaturePython] Screw031  label="M6x14-Screw014"  # Fasteners workbench fastener (typed FeaturePython)
  Placement = pos=(171,108.2,45) rot=(1,0,0;1.5708rad)
  baseObject = -> Washer015 [Edge1]
  diameter = 7
  invert = false
  length = 3
  lengthCustom = 14
  matchOuter = true
  offset = 0
  thread = false
  type = 33
FEATURE [Part::FeaturePython] Screw032  label="M6x14-Screw012"  # Fasteners workbench fastener (typed FeaturePython)
  Placement = pos=(170,50,36.8) rot=(0,0,1;0rad)
  baseObject = -> Washer013 [Edge1]
  diameter = 7
  invert = false
  length = 3
  lengthCustom = 14
  matchOuter = true
  offset = 0
  thread = false
  type = 33
FEATURE [Part::FeaturePython] Screw033  label="M6x14-Screw013"  # Fasteners workbench fastener (typed FeaturePython)
  Placement = pos=(170,36.8,45) rot=(-1,0,0;1.5708rad)
  baseObject = -> Washer012 [Edge1]
  diameter = 7
  invert = false
  length = 3
  lengthCustom = 14
  matchOuter = true
  offset = 0
  thread = false
  type = 33
FEATURE [Part::FeaturePython] Screw034  label="M6x14-Screw008"  # Fasteners workbench fastener (typed FeaturePython)
  Placement = pos=(171,50,303.2) rot=(1,0,0;3.14159rad)
  baseObject = -> Washer008 [Edge1]
  diameter = 7
  invert = false
  length = 3
  lengthCustom = 14
  matchOuter = true
  offset = 0
  thread = false
  type = 33
FEATURE [Part::FeaturePython] Screw035  label="M6x14-Screw009"  # Fasteners workbench fastener (typed FeaturePython)
  Placement = pos=(171,36.8,295) rot=(-1,0,0;1.5708rad)
  baseObject = -> Washer009 [Edge1]
  diameter = 7
  invert = false
  length = 3
  lengthCustom = 14
  matchOuter = true
  offset = 0
  thread = false
  type = 33
FEATURE [Part::FeaturePython] Screw036  label="M6x14-Screw010"  # Fasteners workbench fastener (typed FeaturePython)
  Placement = pos=(171,108.2,290) rot=(1,0,0;1.5708rad)
  baseObject = -> Washer011 [Edge1]
  diameter = 7
  invert = false
  length = 3
  lengthCustom = 14
  matchOuter = true
  offset = 0
  thread = false
  type = 33
FEATURE [Part::FeaturePython] Screw037  label="M6x14-Screw011"  # Fasteners workbench fastener (typed FeaturePython)
  Placement = pos=(171,100,303.2) rot=(1,0,0;3.14159rad)
  baseObject = -> Washer010 [Edge1]
  diameter = 7
  invert = false
  length = 3
  lengthCustom = 14
  matchOuter = true
  offset = 0
  thread = false
  type = 33
FEATURE [Part::FeaturePython] Screw040  label="M6x14-Screw022"  # Fasteners workbench fastener (typed FeaturePython)
  Placement = pos=(149,355,48) rot=(0,-1,0;1.5708rad)
  baseObject = -> Washer023 [Edge1]
  diameter = 7
  invert = false
  length = 3
  lengthCustom = 14
  matchOuter = true
  offset = 0
  thread = false
  type = 33
FEATURE [Part::FeaturePython] Screw041  label="M6x14-Screw023"  # Fasteners workbench fastener (typed FeaturePython)
  Placement = pos=(140,355,36.3) rot=(0,0,1;0rad)
  baseObject = -> Washer022 [Edge1]
  diameter = 7
  invert = false
  length = 3
  lengthCustom = 14
  matchOuter = true
  offset = 0
  thread = false
  type = 33
FEATURE [Part::FeaturePython] Screw042  label="M6x14-Screw021"  # Fasteners workbench fastener (typed FeaturePython)
  Placement = pos=(148.7,355,260) rot=(0,-1,0;1.5708rad)
  baseObject = -> Washer021 [Edge1]
  diameter = 7
  invert = false
  length = 3
  lengthCustom = 14
  matchOuter = true
  offset = 0
  thread = false
  type = 33
FEATURE [Part::FeaturePython] Screw043  label="M6x14-Screw020"  # Fasteners workbench fastener (typed FeaturePython)
  Placement = pos=(137,355,269) rot=(1,0,0;3.14159rad)
  baseObject = -> Washer020 [Edge1]
  diameter = 7
  invert = false
  length = 3
  lengthCustom = 14
  matchOuter = true
  offset = 0
  thread = false
  type = 33
FEATURE [Part::FeaturePython] Screw044  label="M6x14-Screw027"  # Fasteners workbench fastener (typed FeaturePython)
  Placement = pos=(-137,355,269) rot=(1,0,0;3.14159rad)
  baseObject = -> Washer027 [Edge1]
  diameter = 7
  invert = false
  length = 3
  lengthCustom = 14
  matchOuter = true
  offset = 0
  thread = false
  type = 33
FEATURE [Part::FeaturePython] Screw045  label="M6x14-Screw026"  # Fasteners workbench fastener (typed FeaturePython)
  Placement = pos=(-148.7,355,260) rot=(0,1,0;1.5708rad)
  baseObject = -> Washer026 [Edge1]
  diameter = 7
  invert = false
  length = 3
  lengthCustom = 14
  matchOuter = true
  offset = 0
  thread = false
  type = 33
FEATURE [Part::FeaturePython] Screw046  label="M6x14-Screw025"  # Fasteners workbench fastener (typed FeaturePython)
  Placement = pos=(-149,355,48) rot=(0,1,0;1.5708rad)
  baseObject = -> Washer025 [Edge1]
  diameter = 7
  invert = false
  length = 3
  lengthCustom = 14
  matchOuter = true
  offset = 0
  thread = false
  type = 33
FEATURE [Part::FeaturePython] Screw047  label="M6x14-Screw024"  # Fasteners workbench fastener (typed FeaturePython)
  Placement = pos=(-140,355,36.3) rot=(0,0,1;0rad)
  baseObject = -> Washer024 [Edge1]
  diameter = 7
  invert = false
  length = 3
  lengthCustom = 14
  matchOuter = true
  offset = 0
  thread = false
  type = 33
FEATURE [Part::FeaturePython] Screw048  label="M6x14-Screw028"  # Fasteners workbench fastener (typed FeaturePython)
  Placement = pos=(-170,236.8,45) rot=(-1,0,0;1.5708rad)
  baseObject = -> Washer028 [Edge1]
  diameter = 7
  invert = false
  length = 3
  lengthCustom = 14
  matchOuter = true
  offset = 0
  thread = false
  type = 33
FEATURE [Part::FeaturePython] Screw049  label="M6x14-Screw029"  # Fasteners workbench fastener (typed FeaturePython)
  Placement = pos=(-170,250,36.8) rot=(0,0,1;0rad)
  baseObject = -> Washer029 [Edge1]
  diameter = 7
  invert = false
  length = 3
  lengthCustom = 14
  matchOuter = true
  offset = 0
  thread = false
  type = 33
FEATURE [Part::FeaturePython] Screw050  label="M6x14-Screw030"  # Fasteners workbench fastener (typed FeaturePython)
  Placement = pos=(-170,193.2,45) rot=(1,0,0;1.5708rad)
  baseObject = -> Washer031 [Edge1]
  diameter = 7
  invert = false
  length = 3
  lengthCustom = 14
  matchOuter = true
  offset = 0
  thread = false
  type = 33
FEATURE [Part::FeaturePython] Screw051  label="M6x14-Screw031"  # Fasteners workbench fastener (typed FeaturePython)
  Placement = pos=(-170,180,36.8) rot=(0,0,1;0rad)
  baseObject = -> Washer030 [Edge1]
  diameter = 7
  invert = false
  length = 3
  lengthCustom = 14
  matchOuter = true
  offset = 0
  thread = false
  type = 33
FEATURE [Part::FeaturePython] Screw052  label="M6x14-Screw033"  # Fasteners workbench fastener (typed FeaturePython)
  Placement = pos=(-170,66.8,45) rot=(-1,0,0;1.5708rad)
  baseObject = -> Washer033 [Edge1]
  diameter = 7
  invert = false
  length = 3
  lengthCustom = 14
  matchOuter = true
  offset = 0
  thread = false
  type = 33
FEATURE [Part::FeaturePython] Screw053  label="M6x14-Screw032"  # Fasteners workbench fastener (typed FeaturePython)
  Placement = pos=(-170,80,36.8) rot=(0,0,1;0rad)
  baseObject = -> Washer032 [Edge1]
  diameter = 7
  invert = false
  length = 3
  lengthCustom = 14
  matchOuter = true
  offset = 0
  thread = false
  type = 33
FEATURE [Part::FeaturePython] Screw054  label="M6x14-Screw035"  # Fasteners workbench fastener (typed FeaturePython)
  Placement = pos=(-170,185,303.2) rot=(1,0,0;3.14159rad)
  baseObject = -> Washer035 [Edge1]
  diameter = 7
  invert = false
  length = 3
  lengthCustom = 14
  matchOuter = true
  offset = 0
  thread = false
  type = 33
FEATURE [Part::FeaturePython] Screw055  label="M6x14-Screw034"  # Fasteners workbench fastener (typed FeaturePython)
  Placement = pos=(-170,193.2,290) rot=(1,0,0;1.5708rad)
  baseObject = -> Washer034 [Edge1]
  diameter = 7
  invert = false
  length = 3
  lengthCustom = 14
  matchOuter = true
  offset = 0
  thread = false
  type = 33
FEATURE [Part::FeaturePython] Screw056  label="M6x14-Screw061"  # Fasteners workbench fastener (typed FeaturePython)
  Placement = pos=(-140,333.2,485) rot=(1,0,0;1.5708rad)
  baseObject = -> Washer043 [Edge1]
  diameter = 7
  invert = false
  length = 3
  lengthCustom = 14
  matchOuter = true
  offset = 0
  thread = false
  type = 33
FEATURE [Part::FeaturePython] Screw057  label="M6x14-Screw060"  # Fasteners workbench fastener (typed FeaturePython)
  Placement = pos=(-148.2,320,485) rot=(0,1,0;1.5708rad)
  baseObject = -> Washer042 [Edge1]
  diameter = 7
  invert = false
  length = 3
  lengthCustom = 14
  matchOuter = true
  offset = 0
  thread = false
  type = 33
FEATURE [Part::FeaturePython] Screw058  label="M6x14-Screw066"  # Fasteners workbench fastener (typed FeaturePython)
  Placement = pos=(135,333.2,485) rot=(1,0,0;1.5708rad)
  baseObject = -> Washer036 [Edge1]
  diameter = 7
  invert = false
  length = 3
  lengthCustom = 14
  matchOuter = true
  offset = 0
  thread = false
  type = 33
FEATURE [Part::FeaturePython] Screw059  label="M6x14-Screw067"  # Fasteners workbench fastener (typed FeaturePython)
  Placement = pos=(148.2,325,485) rot=(0,-1,0;1.5708rad)
  baseObject = -> Washer037 [Edge1]
  diameter = 7
  invert = false
  length = 3
  lengthCustom = 14
  matchOuter = true
  offset = 0
  thread = false
  type = 33
FEATURE [Part::FeaturePython] Screw060  label="M6x14-Screw073"  # Fasteners workbench fastener (typed FeaturePython)
  Placement = pos=(148.2,50,485) rot=(0,-1,0;1.5708rad)
  baseObject = -> Washer038 [Edge1]
  diameter = 7
  invert = false
  length = 3
  lengthCustom = 14
  matchOuter = true
  offset = 0
  thread = false
  type = 33
FEATURE [Part::FeaturePython] Screw061  label="M6x14-Screw072"  # Fasteners workbench fastener (typed FeaturePython)
  Placement = pos=(140,36.8,485) rot=(-1,0,0;1.5708rad)
  baseObject = -> Washer039 [Edge1]
  diameter = 7
  invert = false
  length = 3
  lengthCustom = 14
  matchOuter = true
  offset = 0
  thread = false
  type = 33
FEATURE [Part::FeaturePython] Screw062  label="M6x14-Screw076"  # Fasteners workbench fastener (typed FeaturePython)
  Placement = pos=(-135,36.8,485) rot=(-1,0,0;1.5708rad)
  baseObject = -> Washer040 [Edge1]
  diameter = 7
  invert = false
  length = 3
  lengthCustom = 14
  matchOuter = true
  offset = 0
  thread = false
  type = 33
FEATURE [Part::FeaturePython] Screw063  label="M6x14-Screw077"  # Fasteners workbench fastener (typed FeaturePython)
  Placement = pos=(-148.2,45,485) rot=(0,1,0;1.5708rad)
  baseObject = -> Washer041 [Edge1]
  diameter = 7
  invert = false
  length = 3
  lengthCustom = 14
  matchOuter = true
  offset = 0
  thread = false
  type = 33
FEATURE [Part::FeaturePython] Screw064  label="M6x14-Screw017"  # Fasteners workbench fastener (typed FeaturePython)
  Placement = pos=(171,151.8,45) rot=(-1,0,0;1.5708rad)
  baseObject = -> Washer017 [Edge1]
  diameter = 7
  invert = false
  length = 3
  lengthCustom = 14
  matchOuter = true
  offset = 0
  thread = false
  type = 33
FEATURE [Part::FeaturePython] Screw065  label="M6x14-Screw016"  # Fasteners workbench fastener (typed FeaturePython)
  Placement = pos=(171,165,36.8) rot=(0,0,1;0rad)
  baseObject = -> Washer016 [Edge1]
  diameter = 7
  invert = false
  length = 3
  lengthCustom = 14
  matchOuter = true
  offset = 0
  thread = false
  type = 33
FEATURE [Part::FeaturePython] Screw066  label="M6x14-Screw019"  # Fasteners workbench fastener (typed FeaturePython)
  Placement = pos=(171,320,36.8) rot=(0,0,1;0rad)
  baseObject = -> Washer018 [Edge1]
  diameter = 7
  invert = false
  length = 3
  lengthCustom = 14
  matchOuter = true
  offset = 0
  thread = false
  type = 33
FEATURE [Part::FeaturePython] Screw067  label="M6x14-Screw018"  # Fasteners workbench fastener (typed FeaturePython)
  Placement = pos=(171,333.2,45) rot=(1,0,0;1.5708rad)
  baseObject = -> Washer019 [Edge1]
  diameter = 7
  invert = false
  length = 3
  lengthCustom = 14
  matchOuter = true
  offset = 0
  thread = false
  type = 33
FEATURE [Part::FeaturePython] Screw068  label="M6x12-Screw002"  # Fasteners workbench fastener (typed FeaturePython)
  Placement = pos=(-170,32,270) rot=(-1,0,0;1.5708rad)
  baseObject = -> Cut008004003004014002002003 [Edge222]
  diameter = 4
  invert = false
  length = 1
  lengthCustom = 12
  matchOuter = false
  offset = -7
  thread = false
  type = 39
FEATURE [Part::FeaturePython] Screw069  label="M6x12-Screw"  # Fasteners workbench fastener (typed FeaturePython)
  Placement = pos=(-170,32,170) rot=(-1,0,0;1.5708rad)
  baseObject = -> Cut008004003004014002002003 [Edge219]
  diameter = 4
  invert = false
  length = 1
  lengthCustom = 12
  matchOuter = false
  offset = -7
  thread = false
  type = 39
FEATURE [Part::FeaturePython] Screw070  label="M6x12-Screw001"  # Fasteners workbench fastener (typed FeaturePython)
  Placement = pos=(-171.336,32.6146,70) rot=(-0.981627,0.190809,0;1.5708rad)
  baseObject = -> Cut008004003004014002002003 [Edge214]
  diameter = 4
  invert = true
  length = 1
  lengthCustom = 12
  matchOuter = false
  offset = -7
  thread = false
  type = 39
FEATURE [Part::Feature] Part__Feature112001094  label="L-corner-bracket023"
  Placement = pos=(-155,355,470) rot=(0.57735,-0.57735,0.57735;4.18879rad)
  shape: bbox 30 x 20 x 30 mm, 10 faces (baked)
FEATURE [Part::Feature] Part__Feature112001095  label="L-corner-bracket024"
  Placement = pos=(-170,340,470) rot=(0,0.707107,-0.707107;3.14159rad)
  shape: bbox 20 x 30 x 30 mm, 10 faces (baked)
FEATURE [Part::Feature] Part__Feature112001096  label="L-corner-bracket025"
  Placement = pos=(-170,30,470) rot=(-1,0,0;1.5708rad)
  shape: bbox 20 x 30 x 30 mm, 10 faces (baked)
FEATURE [Part::Feature] Part__Feature112001097  label="L-corner-bracket026"
  Placement = pos=(170,340,470) rot=(0,0.707107,-0.707107;3.14159rad)
  shape: bbox 20 x 30 x 30 mm, 10 faces (baked)
FEATURE [Part::Feature] Part__Feature112001098  label="L-corner-bracket027"
  Placement = pos=(170,30,470) rot=(-1,0,0;1.5708rad)
  shape: bbox 20 x 30 x 30 mm, 10 faces (baked)
FEATURE [Part::FeaturePython] Washer044  label="M6-Washer110"  # Fasteners workbench fastener (typed FeaturePython)
  Placement = pos=(170,50,465) rot=(1,0,0;3.14159rad)
  baseObject = -> Part__Feature112001098 [Edge1]
  diameter = 2
  invert = true
  matchOuter = true
  offset = 0
  type = 4
FEATURE [Part::FeaturePython] Washer045  label="M6-Washer109"  # Fasteners workbench fastener (typed FeaturePython)
  Placement = pos=(170,35,455) rot=(-1,0,0;1.5708rad)
  baseObject = -> Part__Feature112001098 [Edge7]
  diameter = 2
  invert = true
  matchOuter = true
  offset = 0
  type = 4
FEATURE [Part::FeaturePython] Washer046  label="M6-Washer108"  # Fasteners workbench fastener (typed FeaturePython)
  Placement = pos=(170,320,465) rot=(1,0,0;3.14159rad)
  baseObject = -> Part__Feature112001097 [Edge1]
  diameter = 2
  invert = true
  matchOuter = true
  offset = 0
  type = 4
FEATURE [Part::FeaturePython] Washer047  label="M6-Washer107"  # Fasteners workbench fastener (typed FeaturePython)
  Placement = pos=(170,335,455) rot=(1,0,0;1.5708rad)
  baseObject = -> Part__Feature112001097 [Edge7]
  diameter = 2
  invert = true
  matchOuter = true
  offset = 0
  type = 4
FEATURE [Part::FeaturePython] Washer048  label="M6-Washer103"  # Fasteners workbench fastener (typed FeaturePython)
  Placement = pos=(135,355,465) rot=(1,0,0;3.14159rad)
  baseObject = -> Part__Feature112001075 [Edge1]
  diameter = 2
  invert = true
  matchOuter = true
  offset = 0
  type = 4
FEATURE [Part::FeaturePython] Washer049  label="M6-Washer104"  # Fasteners workbench fastener (typed FeaturePython)
  Placement = pos=(150,355,455) rot=(0,-1,0;1.5708rad)
  baseObject = -> Part__Feature112001075 [Edge7]
  diameter = 2
  invert = true
  matchOuter = true
  offset = 0
  type = 4
FEATURE [Part::FeaturePython] Washer050  label="M6-Washer102"  # Fasteners workbench fastener (typed FeaturePython)
  Placement = pos=(-135,355,465) rot=(1,0,0;3.14159rad)
  baseObject = -> Part__Feature112001094 [Edge1]
  diameter = 2
  invert = true
  matchOuter = true
  offset = 0
  type = 4
FEATURE [Part::FeaturePython] Washer051  label="M6-Washer101"  # Fasteners workbench fastener (typed FeaturePython)
  Placement = pos=(-150,355,455) rot=(0,1,0;1.5708rad)
  baseObject = -> Part__Feature112001094 [Edge7]
  diameter = 2
  invert = true
  matchOuter = true
  offset = 0
  type = 4
FEATURE [Part::FeaturePython] Washer052  label="M6-Washer097"  # Fasteners workbench fastener (typed FeaturePython)
  Placement = pos=(-170,320,465) rot=(1,0,0;3.14159rad)
  baseObject = -> Part__Feature112001095 [Edge4]
  diameter = 2
  invert = true
  matchOuter = true
  offset = 0
  type = 4
FEATURE [Part::FeaturePython] Washer053  label="M6-Washer098"  # Fasteners workbench fastener (typed FeaturePython)
  Placement = pos=(-170,335,455) rot=(1,0,0;1.5708rad)
  baseObject = -> Part__Feature112001095 [Edge7]
  diameter = 2
  invert = true
  matchOuter = true
  offset = 0
  type = 4
FEATURE [Part::FeaturePython] Washer054  label="M6-Washer118"  # Fasteners workbench fastener (typed FeaturePython)
  Placement = pos=(-170,50,465) rot=(1,0,0;3.14159rad)
  baseObject = -> Part__Feature112001096 [Edge1]
  diameter = 2
  invert = true
  matchOuter = true
  offset = 0
  type = 4
FEATURE [Part::FeaturePython] Washer055  label="M6-Washer117"  # Fasteners workbench fastener (typed FeaturePython)
  Placement = pos=(-170,35,455) rot=(-1,0,0;1.5708rad)
  baseObject = -> Part__Feature112001096 [Edge7]
  diameter = 2
  invert = true
  matchOuter = true
  offset = 0
  type = 4
FEATURE [Part::FeaturePython] Screw071  label="M6x14-Screw079"  # Fasteners workbench fastener (typed FeaturePython)
  Placement = pos=(-170,50,463.2) rot=(1,0,0;3.14159rad)
  baseObject = -> Washer054 [Edge1]
  diameter = 7
  invert = false
  length = 3
  lengthCustom = 14
  matchOuter = true
  offset = 0
  thread = false
  type = 33
FEATURE [Part::FeaturePython] Screw072  label="M6x14-Screw078"  # Fasteners workbench fastener (typed FeaturePython)
  Placement = pos=(-170,36.8,455) rot=(-1,0,0;1.5708rad)
  baseObject = -> Washer055 [Edge1]
  diameter = 7
  invert = false
  length = 3
  lengthCustom = 14
  matchOuter = true
  offset = 0
  thread = false
  type = 33
FEATURE [Part::FeaturePython] Screw073  label="M6x14-Screw059"  # Fasteners workbench fastener (typed FeaturePython)
  Placement = pos=(-170,333.2,455) rot=(1,0,0;1.5708rad)
  baseObject = -> Washer053 [Edge1]
  diameter = 7
  invert = false
  length = 3
  lengthCustom = 14
  matchOuter = true
  offset = 0
  thread = false
  type = 33
FEATURE [Part::FeaturePython] Screw074  label="M6x14-Screw058"  # Fasteners workbench fastener (typed FeaturePython)
  Placement = pos=(-170,320,463.2) rot=(1,0,0;3.14159rad)
  baseObject = -> Washer052 [Edge1]
  diameter = 7
  invert = false
  length = 3
  lengthCustom = 14
  matchOuter = true
  offset = 0
  thread = false
  type = 33
FEATURE [Part::FeaturePython] Screw075  label="M6x14-Screw064"  # Fasteners workbench fastener (typed FeaturePython)
  Placement = pos=(135,355,463.2) rot=(1,0,0;3.14159rad)
  baseObject = -> Washer048 [Edge1]
  diameter = 7
  invert = false
  length = 3
  lengthCustom = 14
  matchOuter = true
  offset = 0
  thread = false
  type = 33
FEATURE [Part::FeaturePython] Screw076  label="M6x14-Screw065"  # Fasteners workbench fastener (typed FeaturePython)
  Placement = pos=(148.2,355,455) rot=(0,-1,0;1.5708rad)
  baseObject = -> Washer049 [Edge1]
  diameter = 7
  invert = false
  length = 3
  lengthCustom = 14
  matchOuter = true
  offset = 0
  thread = false
  type = 33
FEATURE [Part::FeaturePython] Screw077  label="M6x14-Screw063"  # Fasteners workbench fastener (typed FeaturePython)
  Placement = pos=(-135,355,463.2) rot=(1,0,0;3.14159rad)
  baseObject = -> Washer050 [Edge1]
  diameter = 7
  invert = false
  length = 3
  lengthCustom = 14
  matchOuter = true
  offset = 0
  thread = false
  type = 33
FEATURE [Part::FeaturePython] Screw078  label="M6x14-Screw062"  # Fasteners workbench fastener (typed FeaturePython)
  Placement = pos=(-148.2,355,455) rot=(0,1,0;1.5708rad)
  baseObject = -> Washer051 [Edge1]
  diameter = 7
  invert = false
  length = 3
  lengthCustom = 14
  matchOuter = true
  offset = 0
  thread = false
  type = 33
FEATURE [Part::FeaturePython] Screw079  label="M6x14-Screw069"  # Fasteners workbench fastener (typed FeaturePython)
  Placement = pos=(170,320,463.2) rot=(1,0,0;3.14159rad)
  baseObject = -> Washer046 [Edge1]
  diameter = 7
  invert = false
  length = 3
  lengthCustom = 14
  matchOuter = true
  offset = 0
  thread = false
  type = 33
FEATURE [Part::FeaturePython] Screw080  label="M6x14-Screw068"  # Fasteners workbench fastener (typed FeaturePython)
  Placement = pos=(170,333.2,455) rot=(1,0,0;1.5708rad)
  baseObject = -> Washer047 [Edge1]
  diameter = 7
  invert = false
  length = 3
  lengthCustom = 14
  matchOuter = true
  offset = 0
  thread = false
  type = 33
FEATURE [Part::FeaturePython] Screw081  label="M6x14-Screw071"  # Fasteners workbench fastener (typed FeaturePython)
  Placement = pos=(170,50,463.2) rot=(1,0,0;3.14159rad)
  baseObject = -> Washer044 [Edge1]
  diameter = 7
  invert = false
  length = 3
  lengthCustom = 14
  matchOuter = true
  offset = 0
  thread = false
  type = 33
FEATURE [Part::FeaturePython] Screw082  label="M6x14-Screw070"  # Fasteners workbench fastener (typed FeaturePython)
  Placement = pos=(170,36.8,455) rot=(-1,0,0;1.5708rad)
  baseObject = -> Washer045 [Edge1]
  diameter = 7
  invert = false
  length = 3
  lengthCustom = 14
  matchOuter = true
  offset = 0
  thread = false
  type = 33
FEATURE [App::Part] Part048  label="frame-bracket"
  Group = -> [Part049,Washer001,Screw028,Screw029,Part__Feature112001040,Washer,Screw026,Screw027,Washer003,Part__Feature112001041,Washer002,Screw025,Screw024,Washer005,Part__Feature112001042,Washer004,Screw023,Screw022,Washer007,Part__Feature008,Washer006,Screw034,Washer009,Screw035,Part__Feature112001083,Washer008,Washer011,Screw036,Screw037,Part__Feature112001082,Washer010,Screw032,Screw033,Washer013,+107 more]
  Origin = -> Origin050
FEATURE [Part::FeaturePython] Screw083  label="M8x20-Screw049"  # Fasteners workbench fastener (typed FeaturePython)
  Placement = pos=(170,130.5,315) rot=(0,0,1;0rad)
  baseObject = -> Part__Feature112001091 [Edge1]
  diameter = 5
  invert = false
  length = 3
  lengthCustom = 20
  matchOuter = true
  offset = 0
  thread = false
  type = 40
FEATURE [Part::FeaturePython] Screw084  label="M8x20-Screw050"  # Fasteners workbench fastener (typed FeaturePython)
  Placement = pos=(-170,214.5,315) rot=(0,0,1;0rad)
  baseObject = -> Part__Feature112001090 [Edge1]
  diameter = 5
  invert = false
  length = 3
  lengthCustom = 20
  matchOuter = true
  offset = 0
  thread = false
  type = 40
FEATURE [Part::FeaturePython] Screw085  label="M8x20-Screw051"  # Fasteners workbench fastener (typed FeaturePython)
  Placement = pos=(-170,214.5,27) rot=(1,0,0;3.14159rad)
  baseObject = -> Part__Feature112001089 [Edge1]
  diameter = 5
  invert = false
  length = 3
  lengthCustom = 20
  matchOuter = true
  offset = 0
  thread = false
  type = 40
FEATURE [Part::FeaturePython] Screw086  label="M8x20-Screw052"  # Fasteners workbench fastener (typed FeaturePython)
  Placement = pos=(170,130.5,27) rot=(1,0,0;3.14159rad)
  baseObject = -> Part__Feature112001092 [Edge1]
  diameter = 5
  invert = false
  length = 3
  lengthCustom = 20
  matchOuter = true
  offset = 0
  thread = false
  type = 40
FEATURE [PartDesign::CoordinateSystem] LCS_main_frame  label="LCS_main-frame"
  AttacherType = Attacher::AttachEngine3D
FEATURE [Part::Feature] Cut001004001  label="3030-500mm-back001-tap-drill"
  Placement = pos=(-170,355,0) rot=(0,0,1;0rad)
  shape: bbox 30 x 30 x 500 mm, 181 faces (baked)
FEATURE [Part::Feature] Cut001002001  label="3030-500mm-front001-tap-drill"
  Placement = pos=(-170,15,0) rot=(0,0,1;0rad)
  shape: bbox 30 x 30 x 500 mm, 167 faces (baked)
FEATURE [Part::Feature] Cut008004003004014002002015  label="3030-500mm-front002-tap-drill"
  Placement = pos=(170,15,0) rot=(0,0,1;0rad)
  shape: bbox 30 x 30 x 500 mm, 167 faces (baked)
FEATURE [Part::Feature] Cut008004003004014002002016  label="3030-500mm-back002-tap-drill"
  Placement = pos=(170,355,0) rot=(0,0,1;0rad)
  shape: bbox 30 x 30 x 500 mm, 181 faces (baked)
FEATURE [App::Part] Part  label="extrusion"
  Group = -> [Extrude002002002002,Extrude002002002003,Cut008004003004014002002003,Screw020,Screw016,Extrude001,Screw013,Screw017,Extrude008,Screw015,Screw011,Cut008004003004014002002011,Screw008,Screw014,Cut008004003004014002002012,Screw012,Screw007,Extrude006,Screw005,Screw010,Extrude002,Screw004,Screw021,Cut008004003004014002002013,Screw003,Screw009,Extrude010,Screw019,Screw002,Cut008004003004014002002014,+17 more]
  Origin = -> Origin
FEATURE [App::Part] Part054  label="main-frame"
  Group = -> [Part048,Part,LCS_main_frame]
  Origin = -> Origin056
